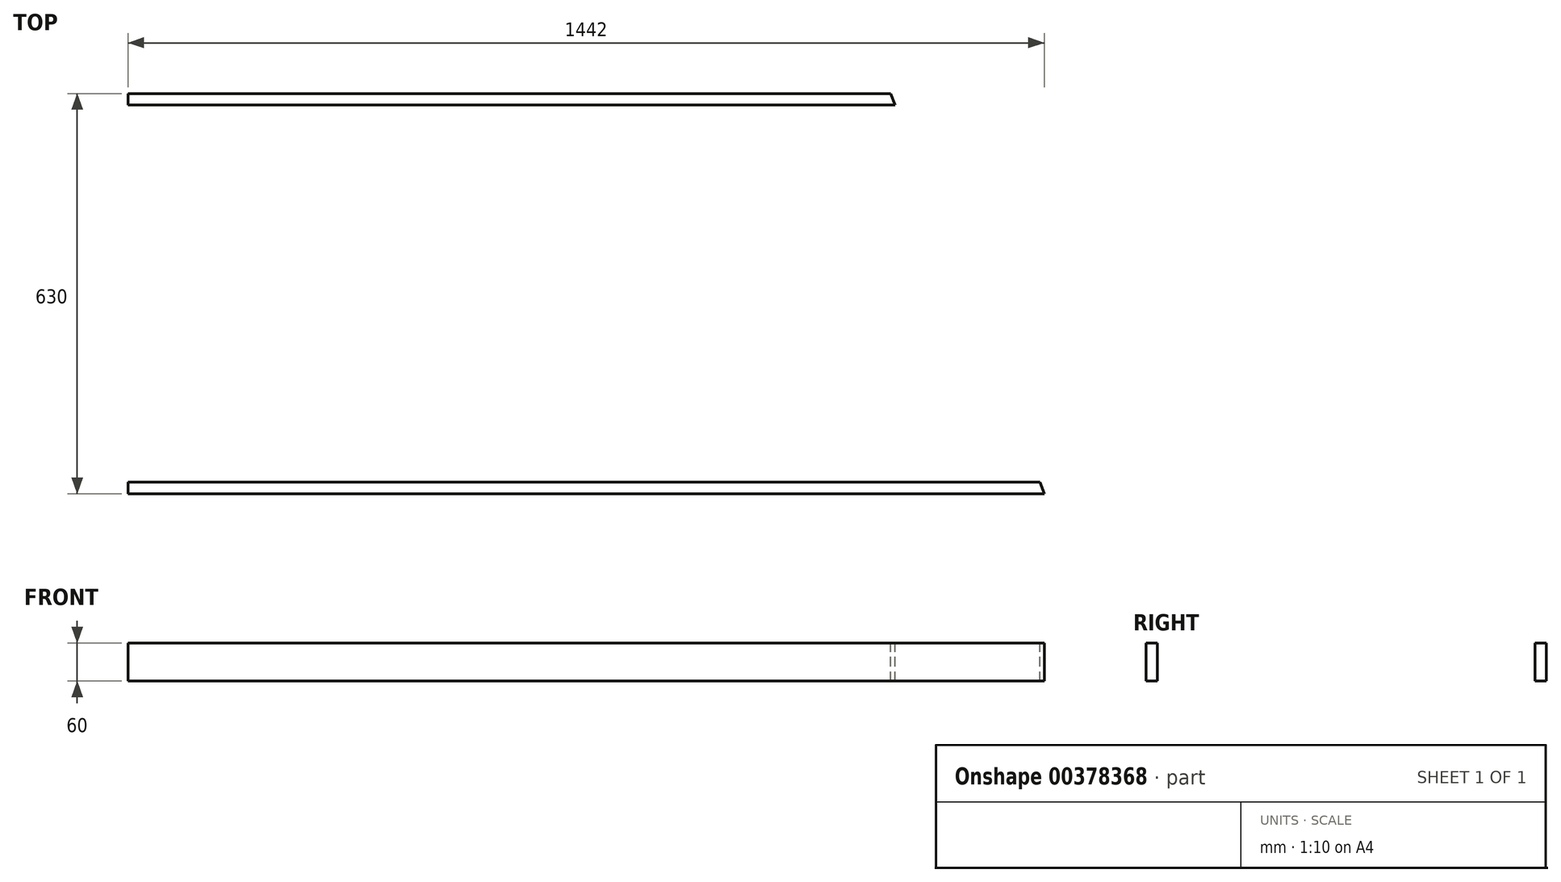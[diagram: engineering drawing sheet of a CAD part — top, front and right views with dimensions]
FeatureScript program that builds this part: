
annotation { "Feature Type Name" : "Feature", "Feature Type Description" : "" }
export const myFeature = defineFeature(function(context is Context, id is Id, definition is map)
    precondition{}
    {
        {
            var Q0;
            Q0=qCreatedBy(makeId("Right.planeOp"),FACE);
            var sketch = newSketch(context, id + "F0", { "sketchPlane" : qUnion([Q0])});
            skLineSegment(sketch, "E0.bottom", {"start": v(9, 30) * mm, "end": v(-9, 30) * mm});
            skLineSegment(sketch, "E0.top", {"start": v(9, -30) * mm, "end": v(-9, -30) * mm});
            skLineSegment(sketch, "E0.left", {"start": v(9, 30) * mm, "end": v(9, -30) * mm});
            skLineSegment(sketch, "E0.right", {"start": v(-9, 30) * mm, "end": v(-9, -30) * mm});
            skPoint(sketch, "E0.middle", {"position": v(0, 0) * mm});
            skLineSegment(sketch, "E1.bottom", {"start": v(603, 30) * mm, "end": v(621, 30) * mm});
            skLineSegment(sketch, "E1.top", {"start": v(603, -30) * mm, "end": v(621, -30) * mm});
            skLineSegment(sketch, "E1.left", {"start": v(603, 30) * mm, "end": v(603, -30) * mm});
            skLineSegment(sketch, "E1.right", {"start": v(621, 30) * mm, "end": v(621, -30) * mm});
            skSolve(sketch);
        }
        {
            var Q0;
            Q0 = qSketchRegion(id + "F0", true);
            extrude(context, id + "F1", {"entities" : qUnion([Q0]), "depth" : 1442 * mm});
        }
        {
            var Q0;
            Q0=qCreatedBy(makeId("Top.planeOp"),FACE);
            var sketch = newSketch(context, id + "F2", { "sketchPlane" : qUnion([Q0])});
            skLineSegment(sketch, "E2", {"start": v(1442, -9) * mm, "end": v(1442, 621) * mm});
            skLineSegment(sketch, "E3", {"start": v(1442, 621) * mm, "end": v(1200.17, 621) * mm});
            skLineSegment(sketch, "E4", {"start": v(1200.17, 621) * mm, "end": v(1442, -9) * mm});
            skSolve(sketch);
        }
        {
            var Q0;
            Q0 = qSketchRegion(id + "F2", true);
            extrude(context, id + "F3", {"entities" : qUnion([Q0]), "operationType" : NewBodyOperationType.REMOVE, "endBound" : BoundingType.SYMMETRIC, "oppositeDirection" : true, "depth" : 140 * mm});
        }
    });
